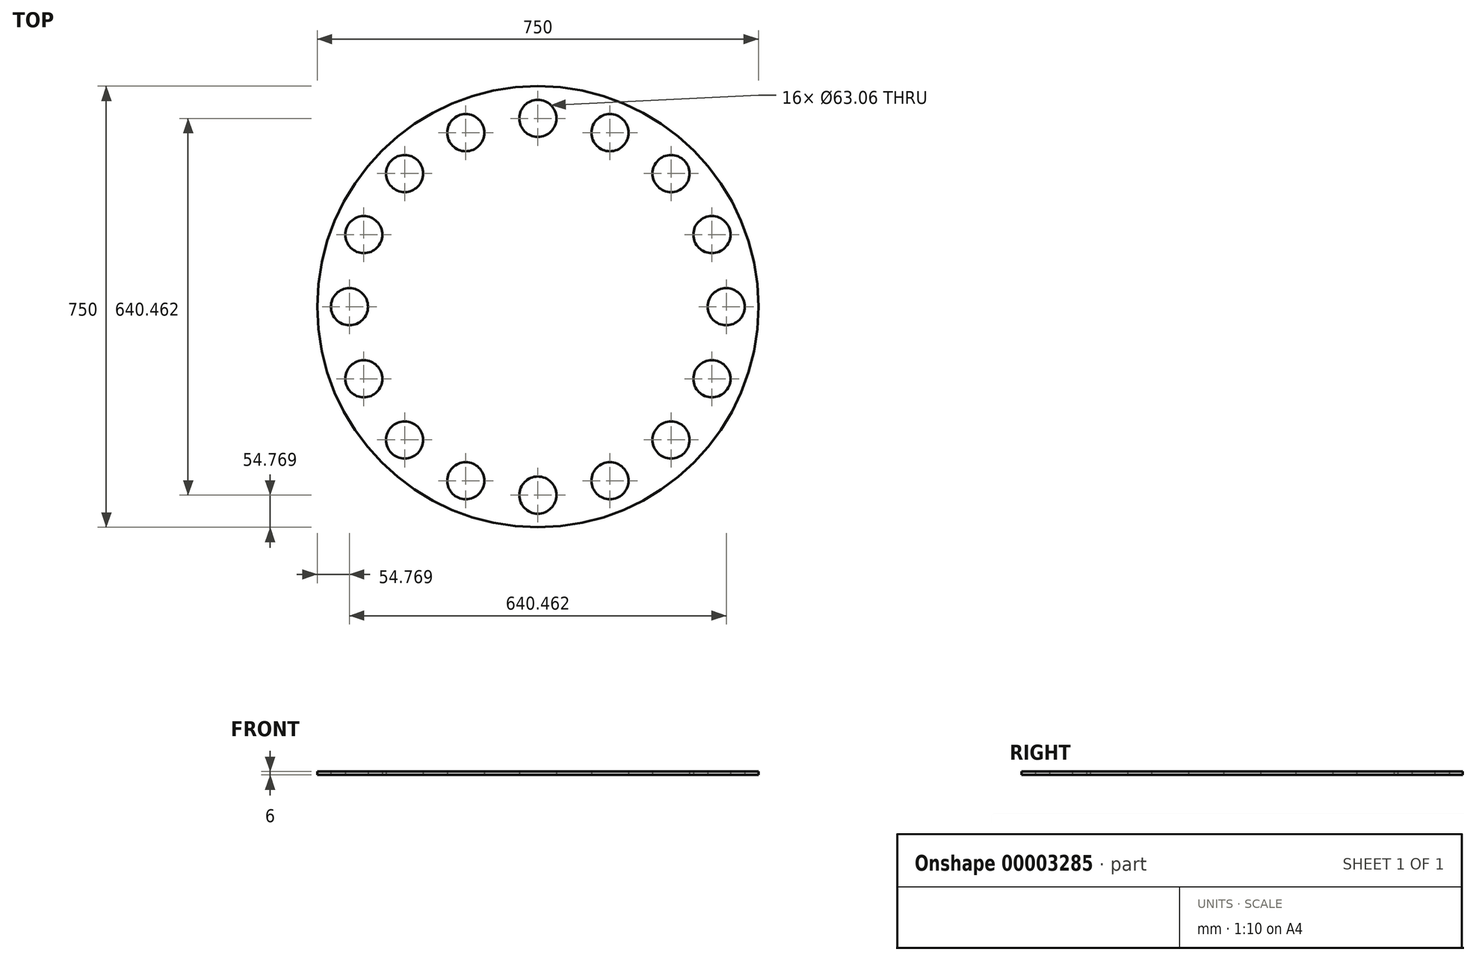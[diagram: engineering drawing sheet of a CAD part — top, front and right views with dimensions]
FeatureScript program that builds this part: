
annotation { "Feature Type Name" : "Feature", "Feature Type Description" : "" }
export const myFeature = defineFeature(function(context is Context, id is Id, definition is map)
    precondition{}
    {
        {
            var Q0;
            Q0=qCreatedBy(makeId("Top.planeOp"),FACE);
            var sketch = newSketch(context, id + "F0", { "sketchPlane" : qUnion([Q0])});
            skCircle(sketch, "E0", {"center": v(0, 0) * mm, "radius": 375 * mm});
            skCircle(sketch, "E1", {"center": v(-320.23, 0) * mm, "radius": 31.53 * mm});
            skSolve(sketch);
        }
        {
            var Q0;
            Q0=makeQuery(id+"F0.imprint","IMPRINT",FACE,{"disambiguationData":[TD([[makeQuery(id+"F0.imprint","IMPRINT",EDGE,{"derivedFrom":sQuery(id+"F0.wireOp",EDGE,"E0")}),1.0]])]});
            extrude(context, id + "F1", {"entities" : qUnion([Q0]), "depth" : 6 * mm});
        }
        {
            var Q0;
            Q0=makeQuery(id+"F1.opExtrude","SWEPT_FACE",FACE,{"disambiguationData":[OSD([sQuery(id+"F0.wireOp",EDGE,"E1")])]});
            var Q1;
            Q1=makeQuery(id+"F1.opExtrude","CAP_EDGE",EDGE,{"disambiguationData":[OSD([sQuery(id+"F0.wireOp",EDGE,"E0")])],"isStart":false});
            circularPattern(context, id + "F2", {"faces" : qUnion([Q0]), "axis" : qUnion([Q1]), "angle" : 360 * degree, "instanceCount" : 16, "equalSpace" : true, "patternType" : PatternType.FACE});
        }
    });
